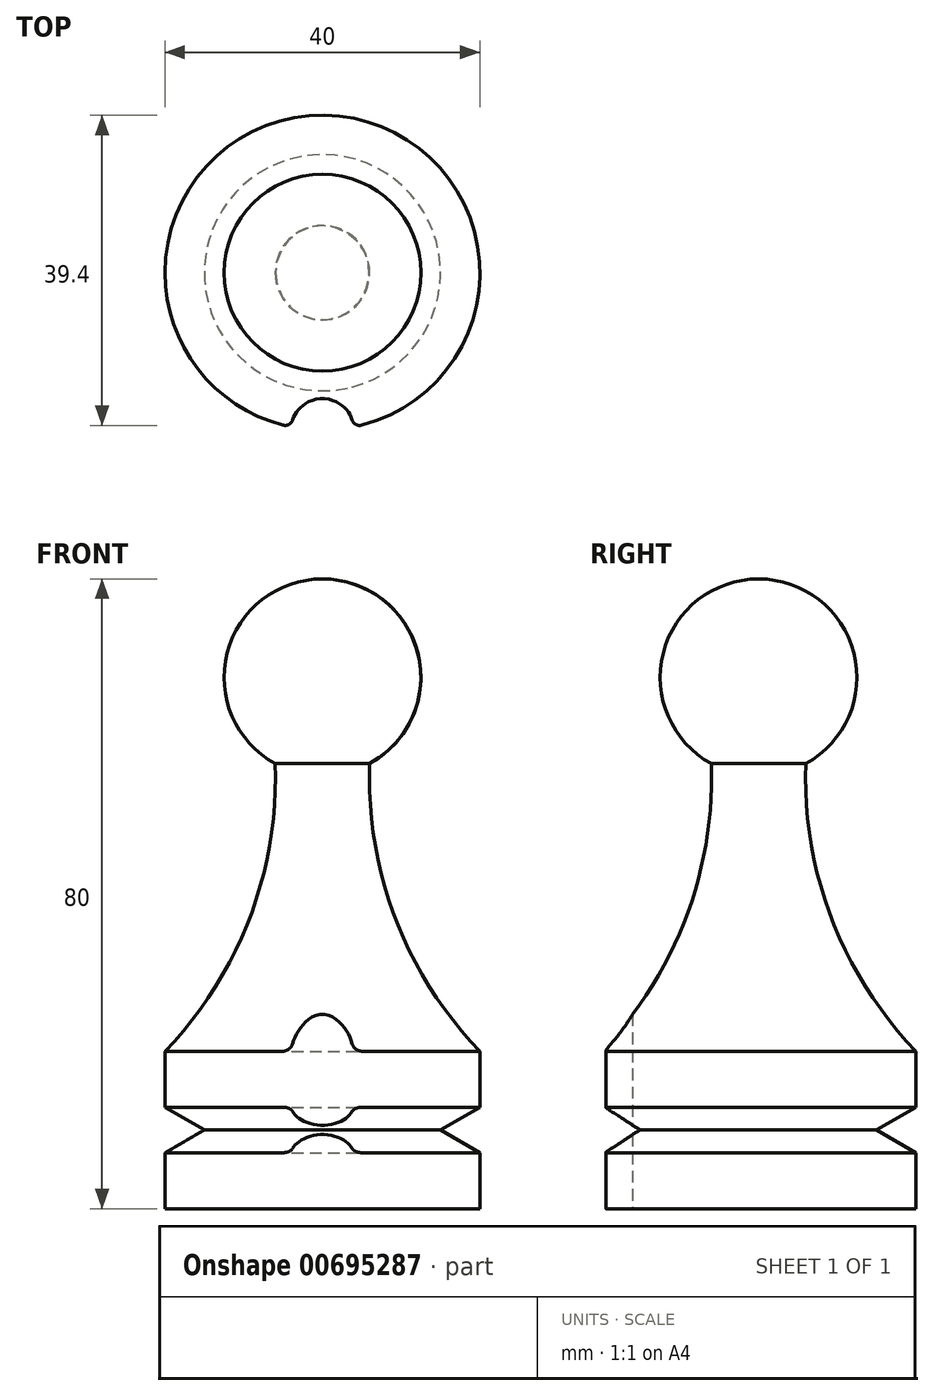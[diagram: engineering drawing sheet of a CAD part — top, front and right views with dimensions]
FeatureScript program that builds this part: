
annotation { "Feature Type Name" : "Feature", "Feature Type Description" : "" }
export const myFeature = defineFeature(function(context is Context, id is Id, definition is map)
    precondition{}
    {
        {
            var Q0;
            Q0=qCreatedBy(makeId("Front.planeOp"),FACE);
            var sketch = newSketch(context, id + "F0", { "sketchPlane" : qUnion([Q0])});
            skLineSegment(sketch, "E0", {"start": v(0, 103.01) * mm, "end": v(0, -62.2) * mm, "construction": true});
            skLineSegment(sketch, "E1", {"start": v(0, -62.2) * mm, "end": v(0, 31.03) * mm, "construction": true});
            skLineSegment(sketch, "E2", {"start": v(0, 0) * mm, "end": v(20, 0) * mm});
            skLineSegment(sketch, "E3", {"start": v(20, 0) * mm, "end": v(20, 12.89) * mm});
            skLineSegment(sketch, "E4", {"start": v(20, 12.89) * mm, "end": v(15, 10) * mm});
            skLineSegment(sketch, "E5", {"start": v(15, 10) * mm, "end": v(20, 7.11) * mm});
            skLineSegment(sketch, "E6", {"start": v(20, 7.11) * mm, "end": v(20, 20) * mm});
            skArc(sketch, "E7", {"start": v(6, 56.53) * mm, "mid": v(9.28, 36.84) * mm, "end": v(20, 20) * mm});
            skArc(sketch, "E8", {"start": v(6, 56.53) * mm, "mid": v(12.11, 70.6) * mm, "end": v(0, 80) * mm});
            skLineSegment(sketch, "E9", {"start": v(0, 80) * mm, "end": v(0, 0) * mm});
            skSolve(sketch);
        }
        {
            var Q0;
            Q0=makeQuery(id+"F0.imprint","IMPRINT",FACE,{"disambiguationData":[TD([[makeQuery(id+"F0.imprint","IMPRINT",EDGE,{"derivedFrom":sQuery(id+"F0.wireOp",EDGE,"E2")}),1.0]])]});
            var Q1;
            Q1=sQuery(id+"F0.wireOp",EDGE,"E1");
            revolve(context, id + "F1", {"surfaceOperationType" : NewSurfaceOperationType.NEW, "entities" : qUnion([Q0]), "axis" : qUnion([Q1]), "revolveType" : RevolveType.FULL});
        }
        {
            var Q0;
            Q0=makeQuery(id+"F1.opRevolve","SWEPT_FACE",FACE,{"disambiguationData":[OSD([sQuery(id+"F0.wireOp",EDGE,"E2")])]});
            var sketch = newSketch(context, id + "F2", { "sketchPlane" : qUnion([Q0])});
            skCircle(sketch, "E10", {"center": v(0, 20) * mm, "radius": 4 * mm});
            skSolve(sketch);
        }
        {
            var Q0;
            Q0 = qSketchRegion(id + "F2", true);
            extrude(context, id + "F3", {"entities" : qUnion([Q0]), "operationType" : NewBodyOperationType.REMOVE, "oppositeDirection" : true, "depth" : 29 * mm, "offsetDistance" : 25 * mm});
        }
        {
            var Q0;
            Q0=makeQuery(id+"F3.boolean.opBoolean","INTERSECT",EDGE,{"disambiguationData":[OD(0.0)],"derivedFrom":[makeQuery(id+"F1.opRevolve","SWEPT_FACE",FACE,{"disambiguationData":[OSD([sQuery(id+"F0.wireOp",EDGE,"E6")])]}),makeQuery(id+"F3.opExtrude","SWEPT_FACE",FACE,{"disambiguationData":[OSD([sQuery(id+"F2.wireOp",EDGE,"E10")])]})]});
            var Q1;
            Q1=makeQuery(id+"F3.boolean.opBoolean","INTERSECT",EDGE,{"disambiguationData":[OD(1.0)],"derivedFrom":[makeQuery(id+"F1.opRevolve","SWEPT_FACE",FACE,{"disambiguationData":[OSD([sQuery(id+"F0.wireOp",EDGE,"E6")])]}),makeQuery(id+"F3.opExtrude","SWEPT_FACE",FACE,{"disambiguationData":[OSD([sQuery(id+"F2.wireOp",EDGE,"E10")])]})]});
            var Q2;
            Q2=makeQuery(id+"F3.boolean.opBoolean","INTERSECT",EDGE,{"disambiguationData":[OD(0.0)],"derivedFrom":[makeQuery(id+"F1.opRevolve","SWEPT_FACE",FACE,{"disambiguationData":[OSD([sQuery(id+"F0.wireOp",EDGE,"E3")])]}),makeQuery(id+"F3.opExtrude","SWEPT_FACE",FACE,{"disambiguationData":[OSD([sQuery(id+"F2.wireOp",EDGE,"E10")])]})]});
            var Q3;
            Q3=makeQuery(id+"F3.boolean.opBoolean","INTERSECT",EDGE,{"disambiguationData":[OD(1.0)],"derivedFrom":[makeQuery(id+"F1.opRevolve","SWEPT_FACE",FACE,{"disambiguationData":[OSD([sQuery(id+"F0.wireOp",EDGE,"E3")])]}),makeQuery(id+"F3.opExtrude","SWEPT_FACE",FACE,{"disambiguationData":[OSD([sQuery(id+"F2.wireOp",EDGE,"E10")])]})]});
            fillet(context, id + "F4", {"entities" : qUnion([Q0, Q1, Q2, Q3]), "radius" : 1 * mm, "tangentPropagation" : true, "allowEdgeOverflow" : false});
        }
    });
